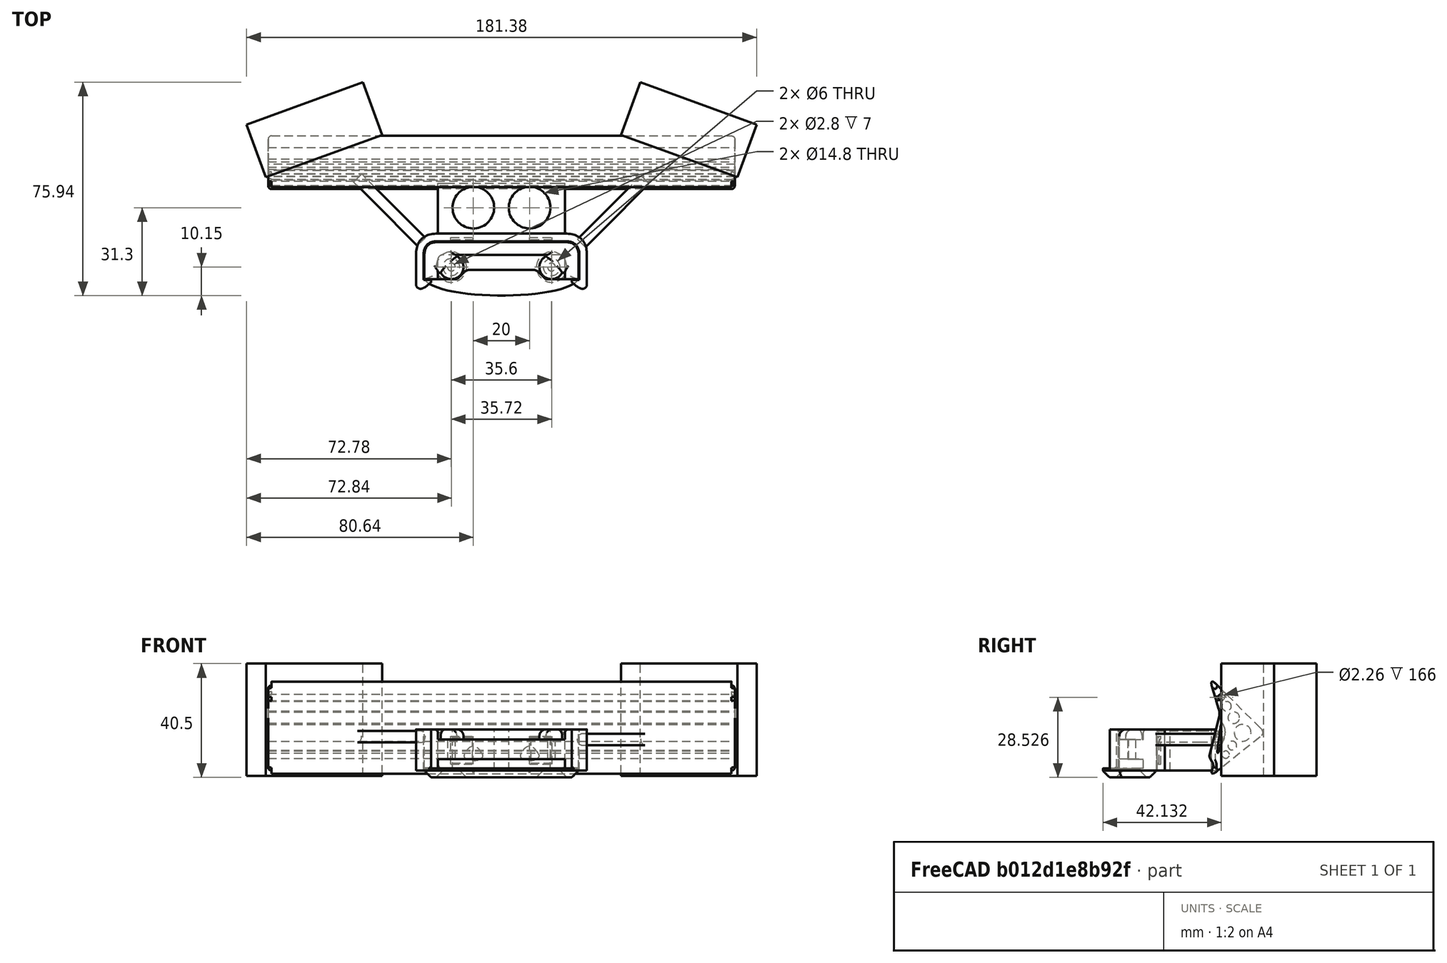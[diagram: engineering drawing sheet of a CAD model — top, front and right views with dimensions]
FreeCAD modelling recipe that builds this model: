
FCSTD DOCUMENT  (FreeCAD 0.21R0.20.1)
Label: 053
License: All rights reserved
LicenseURL: http://en.wikipedia.org/wiki/All_rights_reserved
objects: Part::Cylinder×8, Sketcher::SketchObject×7, Part::Extrusion×7, Part::Box×7, Part::MultiFuse×7, Part::Fillet×7, Part::Cut×4, Part::Chamfer×2
note: 49 computed .brp shape members not serialized (recipe doc carries the construction recipe); baked Part::Feature solids carry a one-line shape summary decoded from their .brp

FEATURE [Sketcher::SketchObject] Sketch  label="attatchmentPiece"
  FullyConstrained = true
  sketch-geometry (20):
    g0: LineSegment StartX=21.05 StartY=0 StartZ=0 EndX=21.05 EndY=-1 EndZ=0
    g1: LineSegment StartX=21.05 StartY=-1 StartZ=0 EndX=21.05 EndY=-4.3 EndZ=0
    g2: LineSegment StartX=-24.15 StartY=4.3 StartZ=0 EndX=21.05 EndY=4.3 EndZ=0
    g3: LineSegment StartX=21.05 StartY=0 StartZ=0 EndX=21.05 EndY=4.3 EndZ=0
    g4-g7: Circle x4 (B-spline internal-alignment scaffolding for g8; pole/knot coordinates omitted)
    g8: BSplineCurve PolesCount=4 KnotsCount=2 Degree=3 IsPeriodic=0
    g9: GeomPoint X=10.05 Y=-1 Z=0
    g10: GeomPoint X=14.55 Y=-4.3 Z=0
    g11: LineSegment StartX=10.05 StartY=-1 StartZ=0 EndX=-10.05 EndY=-1 EndZ=0
    g12: LineSegment StartX=14.55 StartY=-4.3 StartZ=0 EndX=21.05 EndY=-4.3 EndZ=0
    g13: LineSegment StartX=-24.15 StartY=4.3 StartZ=0 EndX=-24.15 EndY=-4.3 EndZ=0
    g14: LineSegment StartX=-13.15 StartY=-1 StartZ=0 EndX=-10.05 EndY=-1 EndZ=0
    g15: LineSegment StartX=-24.15 StartY=-4.3 StartZ=0 EndX=-19.35 EndY=-4.3 EndZ=0
    g16: LineSegment StartX=-19.35 StartY=-4.3 StartZ=0 EndX=-17.65 EndY=-4.3 EndZ=0
    g17: BSplineCurve PolesCount=4 KnotsCount=2 Degree=3 IsPeriodic=0
    g18: Circle CenterX=16.25 CenterY=0 CenterZ=0 NormalX=0 NormalY=0 NormalZ=1 AngleXU=0 Radius=1.4
    g19: Circle CenterX=-19.35 CenterY=0 CenterZ=0 NormalX=0 NormalY=0 NormalZ=1 AngleXU=0 Radius=1.4
  constraints (41):
    c: Vertical(g0)
    c: Coincident(g1,g0)
    c: Vertical(g1)
    c: Block(g0)
    c: Horizontal(g2)
    c: Vertical(g3)
    c: Coincident(g3,g2)
    c: Block(g2)
    c: Block(g3)
    c: Weight(g4) = 1
    c: Equal(g4,g5)
    c: Equal(g4,g6)
    c: Equal(g4,g7)
    c: InternalAlignment(g4-g7 -> g8) x4
    c: InternalAlignment(g9,g8)
    c: InternalAlignment(g10,g8)
    c: Block(g8)
    c: Coincident(g11,g8)
    c: Horizontal(g11)
    c: Coincident(g12,g8)
    c: Coincident(g12,g1)
    c: Horizontal(g12)
    c: Distance(g2) = 45.2
    c: Coincident(g13,g2)
    c: Vertical(g13)
    c: Horizontal(g14)
    c: Distance(g14) = 3.1
    c: Horizontal(g15)
    c: Block(g17)
    c: Coincident(g16,g15)
    c: Coincident(g16,g17)
    c: Horizontal(g16)
    c: Block(g16)
    c: Coincident(g17,g14)
    c: Block(g15)
    c: Block(g11)
    c: Block(g13)
    c: Distance(g15) = 4.8
    c: Distance(g16) = 1.7
    c: Block(g18)
    c: Block(g19)
FEATURE [Part::Extrusion] Extrude  label="attatchmentPiece001"
  Base = -> Sketch
  Dir = (0,0,1)
  DirMode = 2
  FaceMakerClass = Part::FaceMakerBullseye
  LengthFwd = 7
  LengthRev = 0
  Solid = true
  Symmetric = false
FEATURE [Sketcher::SketchObject] Sketch001  label="attatchmentPieceSurround"
  FullyConstrained = true
  sketch-geometry (18):
    g0: LineSegment StartX=25.85 StartY=-4.3 StartZ=0 EndX=21.05 EndY=-4.3 EndZ=0
    g1: LineSegment StartX=25.85 StartY=-4.3 StartZ=0 EndX=25.85 EndY=4.3 EndZ=0
    g2: LineSegment StartX=-21.05 StartY=8.9 StartZ=0 EndX=21.05 EndY=8.9 EndZ=0
    g3: Circle CenterX=21.05 CenterY=8.9 CenterZ=0 NormalX=0 NormalY=0 NormalZ=1 AngleXU=0 Radius=1
    g4: Circle CenterX=25.85 CenterY=8.9 CenterZ=0 NormalX=0 NormalY=0 NormalZ=1 AngleXU=0 Radius=1
    g5: Circle CenterX=25.85 CenterY=4.3 CenterZ=0 NormalX=0 NormalY=0 NormalZ=1 AngleXU=0 Radius=1
    g6: BSplineCurve PolesCount=3 KnotsCount=2 Degree=2 IsPeriodic=0
    g7: GeomPoint X=21.05 Y=8.9 Z=0
    g8: GeomPoint X=25.85 Y=4.3 Z=0
    g9: ArcOfCircle CenterX=19.45 CenterY=2.7 CenterZ=0 NormalX=0 NormalY=0 NormalZ=1 AngleXU=0 Radius=1.6 StartAngle=0 EndAngle=1.5708
    g10: LineSegment StartX=21.05 StartY=2.7 StartZ=0 EndX=21.05 EndY=-4.3 EndZ=0
    g11: BSplineCurve PolesCount=3 KnotsCount=2 Degree=2 IsPeriodic=0
    g12: LineSegment StartX=-28.95 StartY=-4.3 StartZ=0 EndX=-28.95 EndY=4.3 EndZ=0
    g13: LineSegment StartX=-24.15 StartY=-4.3 StartZ=0 EndX=-28.95 EndY=-4.3 EndZ=0
    g14: LineSegment StartX=-24.15 StartY=2.7 StartZ=0 EndX=-24.15 EndY=-4.3 EndZ=0
    g15: ArcOfCircle CenterX=-22.55 CenterY=2.7 CenterZ=0 NormalX=0 NormalY=0 NormalZ=1 AngleXU=0 Radius=1.6 StartAngle=1.5708 EndAngle=3.14159
    g16: LineSegment StartX=-24.15 StartY=8.9 StartZ=0 EndX=-21.05 EndY=8.9 EndZ=0
    g17: LineSegment StartX=-22.55 StartY=4.3 StartZ=0 EndX=19.45 EndY=4.3 EndZ=0
  constraints (38):
    c: Horizontal(g0)
    c: Vertical(g1)
    c: Coincident(g1,g0)
    c: Horizontal(g2)
    c: Distance(g2) = 42.1
    c: Block(g2)
    c: Coincident(g6,g2)
    c: Weight(g3) = 1
    c: Equal(g3,g4)
    c: Equal(g3,g5)
    c: Coincident(g6,g1)
    c: InternalAlignment(g3,g6)
    c: InternalAlignment(g4,g6)
    c: InternalAlignment(g5,g6)
    c: InternalAlignment(g7,g6)
    c: InternalAlignment(g8,g6)
    c: Block(g0)
    c: Block(g6)
    c: Block(g9)
    c: Coincident(g10,g9)
    c: Coincident(g10,g0)
    c: Vertical(g10)
    c: Horizontal(g13)
    c: Coincident(g12,g13)
    c: Vertical(g12)
    c: Coincident(g11,g12)
    c: Block(g12)
    c: Block(g11)
    c: Block(g15)
    c: Coincident(g14,g15)
    c: Coincident(g14,g13)
    c: Vertical(g14)
    c: Coincident(g16,g11)
    c: Coincident(g16,g2)
    c: Horizontal(g16)
    c: Coincident(g17,g15)
    c: Coincident(g17,g9)
    c: Horizontal(g17)
FEATURE [Part::Extrusion] Extrude001  label="attatchmentPieceSurround001"
  Base = -> Sketch001
  Dir = (0,0,1)
  DirMode = 2
  FaceMakerClass = Part::FaceMakerBullseye
  LengthFwd = 14.7
  LengthRev = 0
  Placement = pos=(0,0,-4.1) rot=(0,0,1;0rad)
  Solid = true
  Symmetric = false
FEATURE [Sketcher::SketchObject] Sketch002  label="attatchmentPieceEndScrewHoleCaps"
  FullyConstrained = true
  sketch-geometry (10):
    g0: ArcOfCircle CenterX=16.25 CenterY=0 CenterZ=0 NormalX=0 NormalY=0 NormalZ=1 AngleXU=0 Radius=4.3 StartAngle=2.05456 EndAngle=5.79942
    g1: LineSegment StartX=14.25 StartY=3.80657 StartZ=0 EndX=14.25 EndY=6 EndZ=0
    g2: LineSegment StartX=20.0566 StartY=-2 StartZ=0 EndX=22.25 EndY=-2 EndZ=0
    g3: LineSegment StartX=22.25 StartY=-2 StartZ=0 EndX=22.25 EndY=6 EndZ=0
    g4: LineSegment StartX=14.25 StartY=6 StartZ=0 EndX=22.25 EndY=6 EndZ=0
    g5: LineSegment StartX=-25.35 StartY=-2 StartZ=0 EndX=-25.35 EndY=6 EndZ=0
    g6: LineSegment StartX=-25.35 StartY=-2 StartZ=0 EndX=-23.1566 EndY=-2 EndZ=0
    g7: LineSegment StartX=-17.35 StartY=6 StartZ=0 EndX=-25.35 EndY=6 EndZ=0
    g8: LineSegment StartX=-17.35 StartY=3.80657 StartZ=0 EndX=-17.35 EndY=6 EndZ=0
    g9: ArcOfCircle CenterX=-19.35 CenterY=0 CenterZ=0 NormalX=0 NormalY=0 NormalZ=1 AngleXU=0 Radius=4.3 StartAngle=3.62536 EndAngle=7.37022
  constraints (25):
    c: Block(g0)
    c: Vertical(g1)
    c: Horizontal(g2)
    c: Coincident(g3,g2)
    c: Vertical(g3)
    c: Coincident(g4,g1)
    c: Horizontal(g4)
    c: Coincident(g3,g4)
    c: Block(g4)
    c: Block(g3)
    c: Coincident(g0,g1)
    c: Coincident(g0,g2)
    c: Block(g1)
    c: Block(g9)
    c: Horizontal(g6)
    c: Vertical(g8)
    c: Coincident(g7,g8)
    c: Horizontal(g7)
    c: Coincident(g5,g6)
    c: Vertical(g5)
    c: Coincident(g5,g7)
    c: Block(g7)
    c: Block(g5)
    c: Coincident(g9,g6)
    c: Coincident(g9,g8)
FEATURE [Part::Extrusion] Extrude002  label="attatchmentPieceEndScrewHoleCaps001"
  Base = -> Sketch002
  Dir = (0,0,1)
  DirMode = 2
  FaceMakerClass = Part::FaceMakerBullseye
  LengthFwd = 3.6
  LengthRev = 0
  Placement = pos=(0,0,7) rot=(0,0,1;0rad)
  Solid = true
  Symmetric = false
FEATURE [Sketcher::SketchObject] Sketch003  label="mainBumpperPieceAttatchment"
  FullyConstrained = true
  sketch-geometry (42):
    g0: Circle CenterX=28.85 CenterY=4.3 CenterZ=0 NormalX=0 NormalY=0 NormalZ=1 AngleXU=0 Radius=1
    g1: Circle CenterX=28.85 CenterY=11.9 CenterZ=0 NormalX=0 NormalY=0 NormalZ=1 AngleXU=0 Radius=1
    g2: Circle CenterX=21.05 CenterY=11.9 CenterZ=0 NormalX=0 NormalY=0 NormalZ=1 AngleXU=0 Radius=1
    g3: BSplineCurve PolesCount=3 KnotsCount=2 Degree=2 IsPeriodic=0
    g4: GeomPoint X=28.85 Y=4.3 Z=0
    g5: GeomPoint X=21.05 Y=11.9 Z=0
    g6: LineSegment StartX=-21.05 StartY=11.9 StartZ=0 EndX=21.05 EndY=11.9 EndZ=0
    g7: LineSegment StartX=28.85 StartY=4.3 StartZ=0 EndX=28.85 EndY=-4.3 EndZ=0
    g8: Circle CenterX=21.05 CenterY=9.2 CenterZ=0 NormalX=0 NormalY=0 NormalZ=1 AngleXU=0 Radius=1
    g9: Circle CenterX=26.15 CenterY=9.2 CenterZ=0 NormalX=0 NormalY=0 NormalZ=1 AngleXU=0 Radius=1
    g10: Circle CenterX=26.15 CenterY=4.3 CenterZ=0 NormalX=0 NormalY=0 NormalZ=1 AngleXU=0 Radius=1
    g11: BSplineCurve PolesCount=3 KnotsCount=2 Degree=2 IsPeriodic=0
    g12: GeomPoint X=21.05 Y=9.2 Z=0
    g13: GeomPoint X=26.15 Y=4.3 Z=0
    g14: LineSegment StartX=-21.05 StartY=9.2 StartZ=0 EndX=21.05 EndY=9.2 EndZ=0
    g15: LineSegment StartX=26.15 StartY=-4.3 StartZ=0 EndX=26.15 EndY=4.3 EndZ=0
    g16: LineSegment StartX=26.15 StartY=-4.3 StartZ=0 EndX=26.15 EndY=-4.6 EndZ=0
    g17: LineSegment StartX=23.45 StartY=-4.6 StartZ=0 EndX=26.15 EndY=-4.6 EndZ=0
    g18: LineSegment StartX=28.85 StartY=-4.3 StartZ=0 EndX=28.85 EndY=-7.9 EndZ=0
    g19: LineSegment StartX=23.45 StartY=-4.6 StartZ=0 EndX=23.45 EndY=-5.3 EndZ=0
    g20: Circle CenterX=28.85 CenterY=-7.9 CenterZ=0 NormalX=0 NormalY=0 NormalZ=1 AngleXU=0 Radius=1
    g21: Circle CenterX=26.15 CenterY=-8.2 CenterZ=0 NormalX=0 NormalY=0 NormalZ=1 AngleXU=0 Radius=1
    g22: Circle CenterX=23.45 CenterY=-5.3 CenterZ=0 NormalX=0 NormalY=0 NormalZ=1 AngleXU=0 Radius=1
    g23: BSplineCurve PolesCount=3 KnotsCount=2 Degree=2 IsPeriodic=0
    g24: GeomPoint X=28.85 Y=-7.9 Z=0
    g25: GeomPoint X=23.45 Y=-5.3 Z=0
    g26: LineSegment StartX=-21.05 StartY=9.2 StartZ=0 EndX=-24.15 EndY=9.2 EndZ=0
    g27: BSplineCurve PolesCount=3 KnotsCount=2 Degree=2 IsPeriodic=0
    g28: LineSegment StartX=-29.25 StartY=-4.3 StartZ=0 EndX=-29.25 EndY=-4.6 EndZ=0
    g29: LineSegment StartX=-29.25 StartY=-4.6 StartZ=0 EndX=-26.55 EndY=-4.6 EndZ=0
    g30: LineSegment StartX=-31.95 StartY=-4.3 StartZ=0 EndX=-31.95 EndY=-7.9 EndZ=0
    g31: LineSegment StartX=-26.55 StartY=-4.6 StartZ=0 EndX=-26.55 EndY=-5.3 EndZ=0
    g32: Circle CenterX=-31.95 CenterY=-7.9 CenterZ=0 NormalX=0 NormalY=0 NormalZ=1 AngleXU=0 Radius=1
    g33: Circle CenterX=-29.25 CenterY=-8.2 CenterZ=0 NormalX=0 NormalY=0 NormalZ=1 AngleXU=0 Radius=1
    g34: Circle CenterX=-26.55 CenterY=-5.3 CenterZ=0 NormalX=0 NormalY=0 NormalZ=1 AngleXU=0 Radius=1
    g35: BSplineCurve PolesCount=3 KnotsCount=2 Degree=2 IsPeriodic=0
    g36: GeomPoint X=-31.95 Y=-7.9 Z=0
    g37: GeomPoint X=-26.55 Y=-5.3 Z=0
    g38: LineSegment StartX=-31.95 StartY=4.3 StartZ=0 EndX=-31.95 EndY=-4.3 EndZ=0
    g39: LineSegment StartX=-29.25 StartY=-4.3 StartZ=0 EndX=-29.25 EndY=4.3 EndZ=0
    g40: BSplineCurve PolesCount=3 KnotsCount=2 Degree=2 IsPeriodic=0
    g41: LineSegment StartX=-21.05 StartY=11.9 StartZ=0 EndX=-24.15 EndY=11.9 EndZ=0
  constraints (78):
    c: Weight(g0) = 1
    c: Equal(g0,g1)
    c: Equal(g0,g2)
    c: InternalAlignment(g0,g3)
    c: InternalAlignment(g1,g3)
    c: InternalAlignment(g2,g3)
    c: InternalAlignment(g4,g3)
    c: InternalAlignment(g5,g3)
    c: Block(g3)
    c: Horizontal(g6)
    c: Vertical(g7)
    c: Block(g7)
    c: Block(g6)
    c: Weight(g8) = 1
    c: Equal(g8,g9)
    c: Equal(g8,g10)
    c: InternalAlignment(g8,g11)
    c: InternalAlignment(g9,g11)
    c: InternalAlignment(g10,g11)
    c: InternalAlignment(g12,g11)
    c: InternalAlignment(g13,g11)
    c: Horizontal(g14)
    c: Vertical(g15)
    c: Block(g11)
    c: Block(g15)
    c: Block(g14)
    c: Coincident(g16,g15)
    c: Vertical(g16)
    c: Distance(g16) = 0.3
    c: Horizontal(g17)
    c: Coincident(g17,g16)
    c: Coincident(g18,g7)
    c: Vertical(g18)
    c: Distance(g18) = 3.6
    c: Vertical(g19)
    c: Coincident(g19,g17)
    c: Coincident(g23,g18)
    c: Weight(g20) = 1
    c: Equal(g20,g21)
    c: Equal(g20,g22)
    c: Coincident(g23,g19)
    c: InternalAlignment(g20,g23)
    c: InternalAlignment(g21,g23)
    c: InternalAlignment(g22,g23)
    c: InternalAlignment(g24,g23)
    c: InternalAlignment(g25,g23)
    c: Block(g23)
    c: Horizontal(g26)
    c: Distance(g26) = 3.1
    c: Block(g27)
    c: Vertical(g38)
    c: Block(g38)
    c: Vertical(g39)
    c: Block(g40)
    c: Block(g39)
    c: Vertical(g28)
    c: Coincident(g28,g39)
    c: Coincident(g29,g28)
    c: Horizontal(g29)
    c: Vertical(g30)
    c: Coincident(g30,g38)
    c: Coincident(g31,g29)
    c: Vertical(g31)
    c: Coincident(g35,g30)
    c: Equal(g32,g33)
    c: Equal(g32,g34)
    c: Coincident(g35,g31)
    c: InternalAlignment(g32,g35)
    c: InternalAlignment(g33,g35)
    c: InternalAlignment(g34,g35)
    c: InternalAlignment(g36,g35)
    c: InternalAlignment(g37,g35)
    c: Block(g35)
    c: Coincident(g40,g26)
    c: Block(g29)
    c: Horizontal(g41)
    c: Equal(g26,g41) = 3.1
    c: Coincident(g41,g6)
FEATURE [Part::Box] Box  label="bumpperExtension"
  AttacherType = Attacher::AttachEngine3D
  Height = 14.7
  Length = 45.2
  Placement = pos=(-24.15,11.9,-4.1) rot=(0,0,1;0rad)
  Width = 18
FEATURE [Sketcher::SketchObject] Sketch004  label="bumpperMain"
  FullyConstrained = true
  Placement = pos=(0,0,0) rot=(0.57735,0.57735,0.57735;2.0944rad)
  sketch-geometry (62):
    g0: Circle CenterX=-3.12329 CenterY=2.49901 CenterZ=0 NormalX=0 NormalY=0 NormalZ=1 AngleXU=0 Radius=1
    g1: Circle CenterX=0 CenterY=0 CenterZ=0 NormalX=0 NormalY=0 NormalZ=1 AngleXU=0 Radius=1
    g2: Circle CenterX=-1.35243 CenterY=3.60648 CenterZ=0 NormalX=0 NormalY=0 NormalZ=1 AngleXU=0 Radius=1
    g3: BSplineCurve PolesCount=3 KnotsCount=2 Degree=2 IsPeriodic=0
    g4: GeomPoint X=-3.12329 Y=2.49901 Z=0
    g5: GeomPoint X=-1.35243 Y=3.60648 Z=0
    g6: Circle CenterX=-2.83953 CenterY=33.0261 CenterZ=0 NormalX=0 NormalY=0 NormalZ=1 AngleXU=0 Radius=1
    g7: Circle CenterX=0 CenterY=35.8434 CenterZ=0 NormalX=0 NormalY=0 NormalZ=1 AngleXU=0 Radius=1
    g8: Circle CenterX=-1.15771 CenterY=32.0146 CenterZ=0 NormalX=0 NormalY=0 NormalZ=1 AngleXU=0 Radius=1
    g9: BSplineCurve PolesCount=3 KnotsCount=2 Degree=2 IsPeriodic=0
    g10: GeomPoint X=-2.83953 Y=33.0261 Z=0
    g11: GeomPoint X=-1.15771 Y=32.0146 Z=0
    g12: Circle CenterX=-18.2963 CenterY=17.6904 CenterZ=0 NormalX=0 NormalY=0 NormalZ=1 AngleXU=0 Radius=1
    g13: Circle CenterX=-20 CenterY=16 CenterZ=0 NormalX=0 NormalY=0 NormalZ=1 AngleXU=0 Radius=1
    g14: Circle CenterX=-18.1259 CenterY=14.5008 CenterZ=0 NormalX=0 NormalY=0 NormalZ=1 AngleXU=0 Radius=1
    g15: BSplineCurve PolesCount=3 KnotsCount=2 Degree=2 IsPeriodic=0
    g16: GeomPoint X=-18.2963 Y=17.6904 Z=0
    g17: GeomPoint X=-18.1259 Y=14.5008 Z=0
    g18: LineSegment StartX=-18.2963 StartY=17.6904 StartZ=0 EndX=-2.83953 EndY=33.0261 EndZ=0
    g19: LineSegment StartX=-18.1259 StartY=14.5008 StartZ=0 EndX=-3.12329 EndY=2.49901 EndZ=0
    g20: Circle CenterX=-11.9527 CenterY=16 CenterZ=0 NormalX=0 NormalY=0 NormalZ=1 AngleXU=0 Radius=2.99582
    g21: Circle CenterX=-8.803 CenterY=21.3731 CenterZ=0 NormalX=0 NormalY=0 NormalZ=1 AngleXU=0 Radius=2.03939
    g22: Circle CenterX=-6.23123 CenterY=25.4475 CenterZ=0 NormalX=0 NormalY=0 NormalZ=1 AngleXU=0 Radius=1.69309
    g23: Circle CenterX=-4.38186 CenterY=28.6261 CenterZ=0 NormalX=0 NormalY=0 NormalZ=1 AngleXU=0 Radius=1.13029
    g24: Circle CenterX=-8.28033 CenterY=11.4296 CenterZ=0 NormalX=0 NormalY=0 NormalZ=1 AngleXU=0 Radius=1.57213
    g25: Circle CenterX=-5.93972 CenterY=8.22213 CenterZ=0 NormalX=0 NormalY=0 NormalZ=1 AngleXU=0 Radius=1.28743
    g26: Circle CenterX=-3.47023 CenterY=24.3665 CenterZ=0 NormalX=0 NormalY=0 NormalZ=1 AngleXU=0 Radius=1
    g27: Circle CenterX=-3.90437 CenterY=22.9307 CenterZ=0 NormalX=0 NormalY=0 NormalZ=1 AngleXU=0 Radius=1
    g28: Circle CenterX=-3.53772 CenterY=21.4762 CenterZ=0 NormalX=0 NormalY=0 NormalZ=1 AngleXU=0 Radius=1
    g29: BSplineCurve PolesCount=3 KnotsCount=2 Degree=2 IsPeriodic=0
    g30: GeomPoint X=-3.47023 Y=24.3665 Z=0
    g31: GeomPoint X=-3.53772 Y=21.4762 Z=0
    g32: LineSegment StartX=-1.15771 StartY=32.0146 StartZ=0 EndX=-3.47023 EndY=24.3665 EndZ=0
    g33: Circle CenterX=-5.41867 CenterY=17.9226 CenterZ=0 NormalX=0 NormalY=0 NormalZ=1 AngleXU=0 Radius=1
    g34: Circle CenterX=-6 CenterY=16 CenterZ=0 NormalX=0 NormalY=0 NormalZ=1 AngleXU=0 Radius=1
    g35: Circle CenterX=-5.22753 CenterY=13.9401 CenterZ=0 NormalX=0 NormalY=0 NormalZ=1 AngleXU=0 Radius=1
    g36: BSplineCurve PolesCount=3 KnotsCount=2 Degree=2 IsPeriodic=0
    g37: GeomPoint X=-5.41867 Y=17.9226 Z=0
    g38: GeomPoint X=-5.22753 Y=13.9401 Z=0
    g39: Circle CenterX=-3.98946 CenterY=10.6386 CenterZ=0 NormalX=0 NormalY=0 NormalZ=1 AngleXU=0 Radius=1
    g40: Circle CenterX=-2.58497 CenterY=6.89324 CenterZ=0 NormalX=0 NormalY=0 NormalZ=1 AngleXU=0 Radius=1
    g41: Circle CenterX=-3.11001 CenterY=10.8586 CenterZ=0 NormalX=0 NormalY=0 NormalZ=1 AngleXU=0 Radius=1
    g42: BSplineCurve PolesCount=3 KnotsCount=2 Degree=2 IsPeriodic=0
    g43: GeomPoint X=-3.98946 Y=10.6386 Z=0
    g44: GeomPoint X=-3.11001 Y=10.8586 Z=0
    g45: Circle CenterX=-1.35243 CenterY=3.60648 CenterZ=0 NormalX=0 NormalY=0 NormalZ=1 AngleXU=0 Radius=1
    g46: Circle CenterX=-1.76142 CenterY=4.69712 CenterZ=0 NormalX=0 NormalY=0 NormalZ=1 AngleXU=0 Radius=1
    g47: Circle CenterX=-1.05937 CenterY=5.79125 CenterZ=0 NormalX=0 NormalY=0 NormalZ=1 AngleXU=0 Radius=1
    g48: BSplineCurve PolesCount=3 KnotsCount=2 Degree=2 IsPeriodic=0
    g49: GeomPoint X=-1.35243 Y=3.60648 Z=0
    g50: GeomPoint X=-1.05937 Y=5.79125 Z=0
    g51: Circle CenterX=-0.519336 CenterY=6.6329 CenterZ=0 NormalX=0 NormalY=0 NormalZ=1 AngleXU=0 Radius=1
    g52: Circle CenterX=0 CenterY=7.44228 CenterZ=0 NormalX=0 NormalY=0 NormalZ=1 AngleXU=0 Radius=1
    g53: Circle CenterX=-0.244436 CenterY=8.41194 CenterZ=0 NormalX=0 NormalY=0 NormalZ=1 AngleXU=0 Radius=1
    g54: BSplineCurve PolesCount=3 KnotsCount=2 Degree=2 IsPeriodic=0
    g55: GeomPoint X=-0.519336 Y=6.6329 Z=0
    g56: GeomPoint X=-0.244436 Y=8.41194 Z=0
    g57: LineSegment StartX=-3.53772 StartY=21.4762 StartZ=0 EndX=-0.244436 EndY=8.41194 EndZ=0
    g58: LineSegment StartX=-5.22753 StartY=13.9401 StartZ=0 EndX=-3.98946 EndY=10.6386 EndZ=0
    g59: LineSegment StartX=-1.05937 StartY=5.79125 StartZ=0 EndX=-0.519336 EndY=6.6329 EndZ=0
    g60: BSplineCurve PolesCount=3 KnotsCount=2 Degree=2 IsPeriodic=0
    g61: LineSegment StartX=-4.0304 StartY=17.8099 StartZ=0 EndX=-3.11001 EndY=10.8586 EndZ=0
  constraints (96):
    c: Weight(g0) = 1
    c: Equal(g0,g1)
    c: Equal(g0,g2)
    c: InternalAlignment(g0,g3)
    c: InternalAlignment(g1,g3)
    c: InternalAlignment(g2,g3)
    c: InternalAlignment(g4,g3)
    c: InternalAlignment(g5,g3)
    c: Block(g3)
    c: Weight(g6) = 1
    c: Equal(g6,g7)
    c: Equal(g6,g8)
    c: InternalAlignment(g6,g9)
    c: InternalAlignment(g7,g9)
    c: InternalAlignment(g8,g9)
    c: InternalAlignment(g10,g9)
    c: InternalAlignment(g11,g9)
    c: Block(g9)
    c: Weight(g12) = 1
    c: Equal(g12,g13)
    c: Equal(g12,g14)
    c: InternalAlignment(g12,g15)
    c: InternalAlignment(g13,g15)
    c: InternalAlignment(g14,g15)
    c: InternalAlignment(g16,g15)
    c: InternalAlignment(g17,g15)
    c: Block(g15)
    c: Coincident(g18,g15)
    c: Coincident(g18,g9)
    c: Coincident(g19,g15)
    c: Coincident(g19,g3)
    c: Block(g25)
    c: Block(g24)
    c: Block(g20)
    c: Block(g21)
    c: Block(g22)
    c: Block(g23)
    c: Weight(g26) = 1
    c: Equal(g26,g27)
    c: Equal(g26,g28)
    c: InternalAlignment(g26,g29)
    c: InternalAlignment(g27,g29)
    c: InternalAlignment(g28,g29)
    c: InternalAlignment(g30,g29)
    c: InternalAlignment(g31,g29)
    c: Block(g29)
    c: Coincident(g32,g9)
    c: Coincident(g32,g29)
    c: Weight(g33) = 1
    c: Equal(g33,g34)
    c: Equal(g33,g35)
    c: InternalAlignment(g33,g36)
    c: InternalAlignment(g34,g36)
    c: InternalAlignment(g35,g36)
    c: InternalAlignment(g37,g36)
    c: InternalAlignment(g38,g36)
    c: Block(g36)
    c: Weight(g39) = 1
    c: Equal(g39,g40)
    c: Equal(g39,g41)
    c: InternalAlignment(g39,g42)
    c: InternalAlignment(g40,g42)
    c: InternalAlignment(g41,g42)
    c: InternalAlignment(g43,g42)
    c: InternalAlignment(g44,g42)
    c: Block(g42)
    c: Coincident(g48,g3)
    c: Weight(g45) = 1
    c: Equal(g45,g46)
    c: Equal(g45,g47)
    c: InternalAlignment(g45,g48)
    c: InternalAlignment(g46,g48)
    c: InternalAlignment(g47,g48)
    c: InternalAlignment(g49,g48)
    c: InternalAlignment(g50,g48)
    c: Block(g48)
    c: Weight(g51) = 1
    c: Equal(g51,g52)
    c: Equal(g51,g53)
    c: InternalAlignment(g51,g54)
    c: InternalAlignment(g52,g54)
    c: InternalAlignment(g53,g54)
    c: InternalAlignment(g55,g54)
    c: InternalAlignment(g56,g54)
    c: Block(g54)
    c: Coincident(g57,g29)
    c: Coincident(g57,g54)
    c: Block(g57)
    c: Coincident(g58,g36)
    c: Coincident(g58,g42)
    c: Coincident(g59,g48)
    c: Coincident(g59,g54)
    c: Block(g60)
    c: Coincident(g60,g36)
    c: Coincident(g61,g60)
    c: Coincident(g61,g42)
FEATURE [Part::Extrusion] Extrude004  label="bumpperMain001"
  Base = -> Sketch004
  Dir = (1,0,0)
  DirMode = 2
  FaceMakerClass = Part::FaceMakerBullseye
  LengthFwd = 166
  LengthRev = 0
  Placement = pos=(81.45,27.6,-6.6) rot=(0,0,1;3.14159rad)
  Solid = true
  Symmetric = false
FEATURE [Sketcher::SketchObject] Sketch005  label="attatchmentPieceBottom"
  FullyConstrained = true
  sketch-geometry (20):
    g0: LineSegment StartX=25.85 StartY=-4.3 StartZ=0 EndX=25.85 EndY=4.3 EndZ=0
    g1: LineSegment StartX=-21.05 StartY=8.9 StartZ=0 EndX=21.05 EndY=8.9 EndZ=0
    g2: Circle CenterX=21.05 CenterY=8.9 CenterZ=0 NormalX=0 NormalY=0 NormalZ=1 AngleXU=0 Radius=1
    g3: Circle CenterX=25.85 CenterY=8.9 CenterZ=0 NormalX=0 NormalY=0 NormalZ=1 AngleXU=0 Radius=1
    g4: Circle CenterX=25.85 CenterY=4.3 CenterZ=0 NormalX=0 NormalY=0 NormalZ=1 AngleXU=0 Radius=1
    g5: BSplineCurve PolesCount=3 KnotsCount=2 Degree=2 IsPeriodic=0
    g6: GeomPoint X=21.05 Y=8.9 Z=0
    g7: GeomPoint X=25.85 Y=4.3 Z=0
    g8: BSplineCurve PolesCount=3 KnotsCount=2 Degree=2 IsPeriodic=0
    g9: LineSegment StartX=-28.95 StartY=-4.3 StartZ=0 EndX=-28.95 EndY=4.3 EndZ=0
    g10: LineSegment StartX=-24.15 StartY=8.9 StartZ=0 EndX=-21.05 EndY=8.9 EndZ=0
    g11: Circle CenterX=-19.41 CenterY=0 CenterZ=0 NormalX=0 NormalY=0 NormalZ=1 AngleXU=0 Radius=3
    g12: Circle CenterX=16.3103 CenterY=0 CenterZ=0 NormalX=0 NormalY=0 NormalZ=1 AngleXU=0 Radius=3
    g13-g16: Circle x4 (B-spline internal-alignment scaffolding for g17; pole/knot coordinates omitted)
    g17: BSplineCurve PolesCount=4 KnotsCount=2 Degree=3 IsPeriodic=0
    g18: GeomPoint X=-28.95 Y=-4.3 Z=0
    g19: GeomPoint X=25.85 Y=-4.3 Z=0
  constraints (36):
    c: Vertical(g0)
    c: Horizontal(g1)
    c: Distance(g1) = 42.1
    c: Block(g1)
    c: Coincident(g5,g1)
    c: Weight(g2) = 1
    c: Equal(g2,g3)
    c: Equal(g2,g4)
    c: Coincident(g5,g0)
    c: InternalAlignment(g2,g5)
    c: InternalAlignment(g3,g5)
    c: InternalAlignment(g4,g5)
    c: InternalAlignment(g6,g5)
    c: InternalAlignment(g7,g5)
    c: Block(g5)
    c: Vertical(g9)
    c: Coincident(g8,g9)
    c: Block(g9)
    c: Block(g8)
    c: Coincident(g10,g8)
    c: Coincident(g10,g1)
    c: Horizontal(g10)
    c: PointOnObject(g12,g-1)
    c: PointOnObject(g11,g-1)
    c: Block(g11)
    c: Block(g12)
    c: Coincident(g17,g9)
    c: Weight(g13) = 1
    c: Equal(g13,g14)
    c: Equal(g13,g15)
    c: Equal(g13,g16)
    c: Coincident(g17,g0)
    c: InternalAlignment(g13-g16 -> g17) x4
    c: InternalAlignment(g18,g17)
    c: InternalAlignment(g19,g17)
    c: Block(g17)
FEATURE [Part::Extrusion] Extrude005  label="removeFromMainBumpperPieceAttatchment"
  Base = -> Sketch005
  Dir = (0,0,1)
  DirMode = 2
  FaceMakerClass = Part::FaceMakerBullseye
  LengthFwd = 3.2
  LengthRev = 0
  Placement = pos=(0,0,-6.2) rot=(0,0,1;0rad)
  Solid = true
  Symmetric = false
FEATURE [Part::Extrusion] Extrude006  label="mainBumpperPieceAttatchment001"
  Base = -> Sketch003
  Dir = (0,0,1)
  DirMode = 2
  FaceMakerClass = Part::FaceMakerBullseye
  LengthFwd = 14.7
  LengthRev = 0
  Placement = pos=(0,0,-4.1) rot=(0,0,1;0rad)
  Solid = true
  Symmetric = false
FEATURE [Part::Cylinder] Cylinder  label="removeFromBumpperExtension"
  Angle = 360
  AttacherType = Attacher::AttachEngine3D
  FirstAngle = 0
  Height = 20
  Placement = pos=(8.45,21.15,-8) rot=(0,0,1;0rad)
  Radius = 7.4
  SecondAngle = 0
FEATURE [Part::Cylinder] Cylinder001  label="removeFromBumpperExtension001"
  Angle = 360
  AttacherType = Attacher::AttachEngine3D
  FirstAngle = 0
  Height = 20
  Placement = pos=(-11.55,21.15,-8) rot=(0,0,1;0rad)
  Radius = 7.4
  SecondAngle = 0
FEATURE [Part::MultiFuse] Fusion  label="removeFromBumpperExtension002"
  Shapes = -> [Cylinder,Cylinder001]
FEATURE [Part::Cylinder] Cylinder002  label="removeFromBumpperExtension004"
  Angle = 360
  AttacherType = Attacher::AttachEngine3D
  FirstAngle = 0
  Height = 20
  Placement = pos=(8.45,21.15,-8) rot=(0,0,1;0rad)
  Radius = 7.4
  SecondAngle = 0
FEATURE [Part::Cylinder] Cylinder003  label="removeFromBumpperExtension005"
  Angle = 360
  AttacherType = Attacher::AttachEngine3D
  FirstAngle = 0
  Height = 20
  Placement = pos=(-11.55,21.15,-8) rot=(0,0,1;0rad)
  Radius = 7.4
  SecondAngle = 0
FEATURE [Part::MultiFuse] Fusion001  label="removeFromBumpperMain"
  Shapes = -> [Cylinder002,Cylinder003]
FEATURE [Part::Cut] Cut  label="bumpperExtension001"
  Base = -> Box
  Tool = -> Fusion
FEATURE [Part::Fillet] Fillet  label="bumpperExtension002"
  Base = -> Cut
  Edges = 4 edges r=3: [Edge2,Edge4,Edge9,Edge14]
FEATURE [Part::Box] Box001  label="bumpperExtensionBumpHole"
  AttacherType = Attacher::AttachEngine3D
  Height = 10
  Length = 8
  Placement = pos=(8.45,9.2,-1.8) rot=(0,0,1;0rad)
  Width = 1.3
FEATURE [Part::Box] Box002  label="bumpperExtensionBumpHole001"
  AttacherType = Attacher::AttachEngine3D
  Height = 10
  Length = 8
  Placement = pos=(-19.55,9.2,-1.8) rot=(0,0,1;0rad)
  Width = 1.3
FEATURE [Part::Box] Box003  label="attatchmentPieceSurroundBump"
  AttacherType = Attacher::AttachEngine3D
  Height = 9.2
  Length = 7.2
  Placement = pos=(8.85,8.9,-1.4) rot=(0,0,1;0rad)
  Width = 1.3
FEATURE [Part::Box] Box004  label="attatchmentPieceSurroundBump001"
  AttacherType = Attacher::AttachEngine3D
  Height = 9.2
  Length = 7.2
  Placement = pos=(-19.15,8.9,-1.4) rot=(0,0,1;0rad)
  Width = 1.3
FEATURE [Part::MultiFuse] Fusion002  label="attatchmentPieceSurroundBump002"
  Placement = pos=(0,-0.4,0) rot=(0,0,1;0rad)
  Shapes = -> [Box004,Box003]
FEATURE [Part::MultiFuse] Fusion003  label="bumpperExtensionBumpHole002"
  Shapes = -> [Box002,Box001]
FEATURE [Part::Cut] Cut002  label="mainBumpperPieceAttatchment002"
  Base = -> Extrude006
  Tool = -> Fusion003
FEATURE [Part::Fillet] Fillet003  label="attatchmentPieceEndScrewHoleCaps002"
  Base = -> Extrude002
  Edges = 6 edges r=2.4: [Edge4,Edge7,Edge15,Edge25,Edge28,Edge30]
FEATURE [Part::Fillet] Fillet004  label="attatchmentPieceSurround002"
  Base = -> Extrude001
  Edges = 3 edges r=1.2: [Edge19,Edge25,Edge31]
FEATURE [Part::Fillet] Fillet006  label="mainBumpperPieceAttatchment003"
  Base = -> Cut002
  Edges = 2 edges r=1.6: [Edge2,Edge55]
FEATURE [Sketcher::SketchObject] Sketch006  label="attatchmentPieceBottom002"
  FullyConstrained = true
  sketch-geometry (20):
    g0: LineSegment StartX=25.85 StartY=-4.3 StartZ=0 EndX=25.85 EndY=4.3 EndZ=0
    g1: LineSegment StartX=-21.05 StartY=8.9 StartZ=0 EndX=21.05 EndY=8.9 EndZ=0
    g2: Circle CenterX=21.05 CenterY=8.9 CenterZ=0 NormalX=0 NormalY=0 NormalZ=1 AngleXU=0 Radius=1
    g3: Circle CenterX=25.85 CenterY=8.9 CenterZ=0 NormalX=0 NormalY=0 NormalZ=1 AngleXU=0 Radius=1
    g4: Circle CenterX=25.85 CenterY=4.3 CenterZ=0 NormalX=0 NormalY=0 NormalZ=1 AngleXU=0 Radius=1
    g5: BSplineCurve PolesCount=3 KnotsCount=2 Degree=2 IsPeriodic=0
    g6: GeomPoint X=21.05 Y=8.9 Z=0
    g7: GeomPoint X=25.85 Y=4.3 Z=0
    g8: BSplineCurve PolesCount=3 KnotsCount=2 Degree=2 IsPeriodic=0
    g9: LineSegment StartX=-28.95 StartY=-4.3 StartZ=0 EndX=-28.95 EndY=4.3 EndZ=0
    g10: LineSegment StartX=-24.15 StartY=8.9 StartZ=0 EndX=-21.05 EndY=8.9 EndZ=0
    g11: Circle CenterX=-19.41 CenterY=0 CenterZ=0 NormalX=0 NormalY=0 NormalZ=1 AngleXU=0 Radius=3
    g12: Circle CenterX=16.3103 CenterY=0 CenterZ=0 NormalX=0 NormalY=0 NormalZ=1 AngleXU=0 Radius=3
    g13-g16: Circle x4 (B-spline internal-alignment scaffolding for g17; pole/knot coordinates omitted)
    g17: BSplineCurve PolesCount=4 KnotsCount=2 Degree=3 IsPeriodic=0
    g18: GeomPoint X=-28.95 Y=-4.3 Z=0
    g19: GeomPoint X=25.85 Y=-4.3 Z=0
  constraints (36):
    c: Vertical(g0)
    c: Horizontal(g1)
    c: Distance(g1) = 42.1
    c: Block(g1)
    c: Coincident(g5,g1)
    c: Weight(g2) = 1
    c: Equal(g2,g3)
    c: Equal(g2,g4)
    c: Coincident(g5,g0)
    c: InternalAlignment(g2,g5)
    c: InternalAlignment(g3,g5)
    c: InternalAlignment(g4,g5)
    c: InternalAlignment(g6,g5)
    c: InternalAlignment(g7,g5)
    c: Block(g5)
    c: Vertical(g9)
    c: Coincident(g8,g9)
    c: Block(g9)
    c: Block(g8)
    c: Coincident(g10,g8)
    c: Coincident(g10,g1)
    c: Horizontal(g10)
    c: PointOnObject(g12,g-1)
    c: PointOnObject(g11,g-1)
    c: Block(g11)
    c: Block(g12)
    c: Coincident(g17,g9)
    c: Weight(g13) = 1
    c: Equal(g13,g14)
    c: Equal(g13,g15)
    c: Equal(g13,g16)
    c: Coincident(g17,g0)
    c: InternalAlignment(g13-g16 -> g17) x4
    c: InternalAlignment(g18,g17)
    c: InternalAlignment(g19,g17)
    c: Block(g17)
FEATURE [Part::Extrusion] Extrude007  label="attatchmentPieceBottom003"
  Base = -> Sketch006
  Dir = (0,0,1)
  DirMode = 2
  FaceMakerClass = Part::FaceMakerBullseye
  LengthFwd = 3.2
  LengthRev = 0
  Placement = pos=(0,0,-6.5) rot=(0,0,1;0rad)
  Solid = true
  Symmetric = false
FEATURE [Part::Cut] Cut003  label="mainBumpperPieceAttatchment004"
  Base = -> Fillet006
  Tool = -> Extrude005
FEATURE [Part::Chamfer] Chamfer
  Base = -> Extrude007
  Edges = 2 edges r=2.4: [Edge23,Edge26]
FEATURE [Part::Chamfer] Chamfer001  label="attatchmentPieceBottom004"
  Base = -> Chamfer
  Edges = 7 edges r=2.4: [Edge14,Edge15,Edge16,Edge17,Edge18,Edge19,Edge20]
FEATURE [Part::Fillet] Fillet007  label="attatchmentPieceBottom005"
  Base = -> Chamfer001
  Edges = 7 edges r=1.2: [Edge1,Edge2,Edge3,Edge4,Edge5,Edge6,Edge7]
FEATURE [Part::MultiFuse] Fusion007  label="attatchment"
  Shapes = -> [Fillet007,Fillet004,Fillet003,Fusion002,Extrude]
FEATURE [Part::Cut] Cut001  label="bumpperMain002"
  Base = -> Extrude004
  Tool = -> Fusion001
FEATURE [Part::Fillet] Fillet001
  Base = -> Cut001
  Edges = 11 edges r=1.2: [Edge4,Edge7,Edge10,Edge30,Edge31,Edge32,Edge33,Edge34,Edge35,Edge36,Edge37]
FEATURE [Part::Fillet] Fillet002  label="bumpperMain003"
  Base = -> Fillet001
  Edges = 11 edges r=1.2: [Edge4,Edge9,Edge13,Edge14,Edge15,Edge16,Edge17,Edge18,Edge19,Edge20,Edge21]
FEATURE [Part::Cylinder] Cylinder004  label="brace"
  Angle = 360
  AttacherType = Attacher::AttachEngine3D
  FirstAngle = 0
  Height = 32
  Placement = pos=(-42,0,0) rot=(0,1,0;1.5708rad)
  Radius = 2
  SecondAngle = 0
FEATURE [Part::Cylinder] Cylinder005  label="brace001"
  Angle = 360
  AttacherType = Attacher::AttachEngine3D
  FirstAngle = 0
  Height = 10
  Placement = pos=(29,0,0) rot=(0,1,0;1.5708rad)
  Radius = 2
  SecondAngle = 0
FEATURE [Part::Cylinder] Cylinder006  label="brace002"
  Angle = 360
  AttacherType = Attacher::AttachEngine3D
  FirstAngle = 0
  Height = 10
  Placement = pos=(-42,0,0) rot=(0,1,0;1.5708rad)
  Radius = 2
  SecondAngle = 0
FEATURE [Part::MultiFuse] Fusion008  label="leftBrace"
  Placement = pos=(-23,2,8) rot=(0,0,1;-0.785398rad)
  Shapes = -> [Cylinder004,Cylinder006]
FEATURE [Part::Cylinder] Cylinder007  label="brace003"
  Angle = 360
  AttacherType = Attacher::AttachEngine3D
  FirstAngle = 0
  Height = 32
  Placement = pos=(29,0,0) rot=(0,1,0;1.5708rad)
  Radius = 2
  SecondAngle = 0
FEATURE [Part::MultiFuse] Fusion009  label="rightBrace"
  Placement = pos=(6.4,-12,7) rot=(0,0,1;0.785398rad)
  Shapes = -> [Cylinder007,Cylinder005]
FEATURE [Part::Box] Box005  label="Cube"
  AttacherType = Attacher::AttachEngine3D
  Height = 40
  Length = 44
  Placement = pos=(41,47,-6) rot=(0,0,1;-0.349066rad)
  Width = 20
FEATURE [Part::Box] Box006  label="Cube001"
  AttacherType = Attacher::AttachEngine3D
  Height = 40
  Length = 44
  Placement = pos=(-85.35,31.95,-6) rot=(0,0,1;0.349066rad)
  Width = 20
